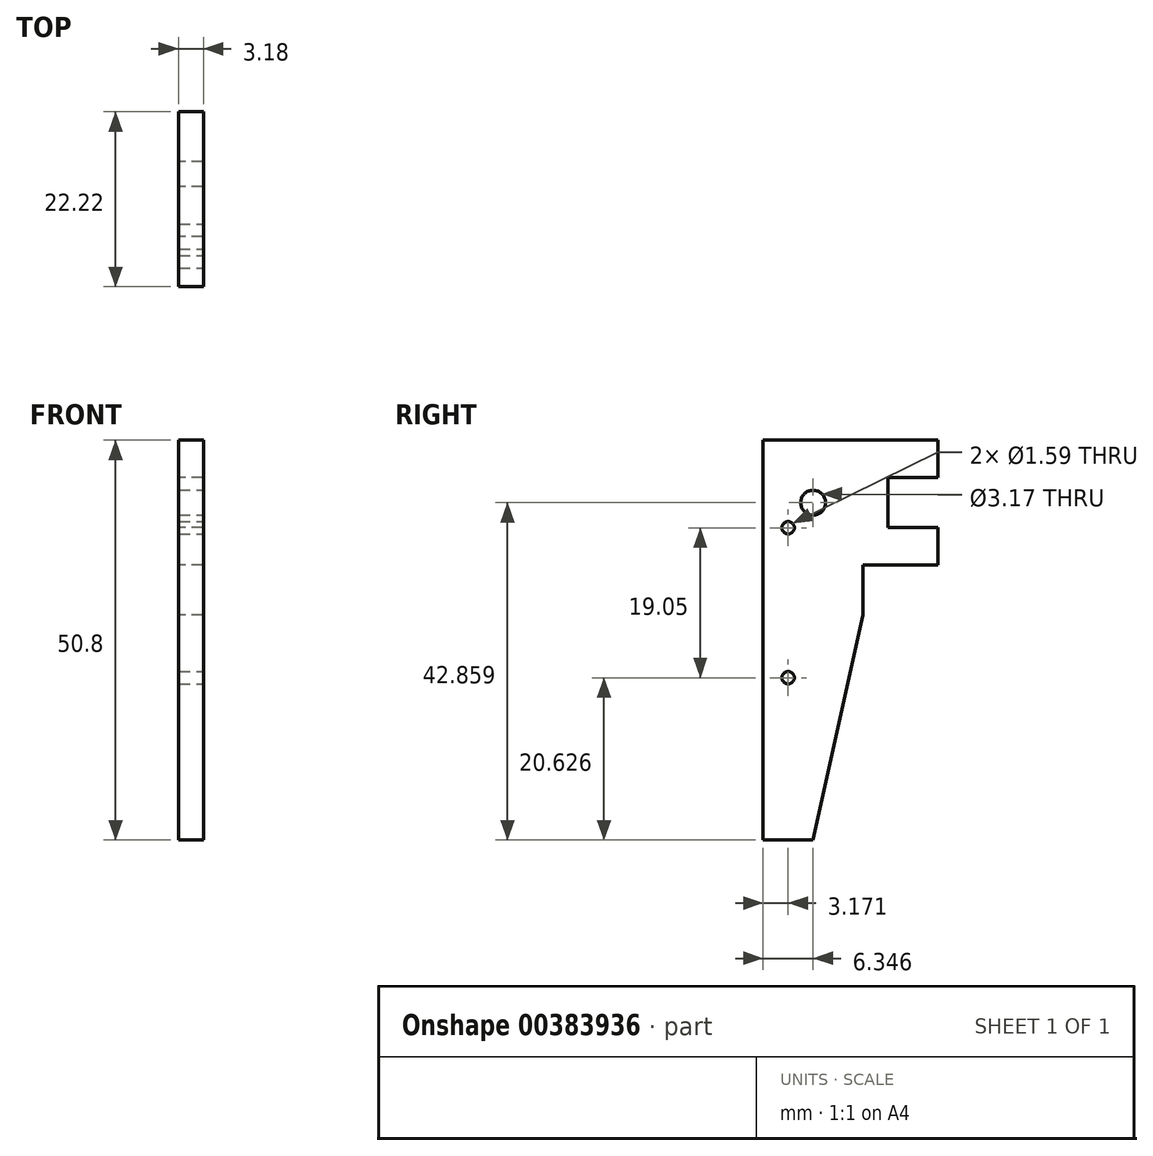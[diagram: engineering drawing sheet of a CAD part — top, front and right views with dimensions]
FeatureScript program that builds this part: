
annotation { "Feature Type Name" : "Feature", "Feature Type Description" : "" }
export const myFeature = defineFeature(function(context is Context, id is Id, definition is map)
    precondition{}
    {
        {
            var Q0;
            Q0=qCreatedBy(makeId("Right.planeOp"),FACE);
            var sketch = newSketch(context, id + "F0", { "sketchPlane" : qUnion([Q0])});
            skPoint(sketch, "E0.middle", {"position": v(-29.23, 59.86) * mm});
            skLineSegment(sketch, "E1", {"start": v(-22.88, 64.62) * mm, "end": v(-13.36, 64.62) * mm});
            skLineSegment(sketch, "E2", {"start": v(-13.36, 80.5) * mm, "end": v(-13.36, 75.73) * mm});
            skLineSegment(sketch, "E3", {"start": v(-13.36, 64.62) * mm, "end": v(-13.36, 69.38) * mm});
            skLineSegment(sketch, "E4", {"start": v(-13.36, 75.73) * mm, "end": v(-19.7, 75.73) * mm});
            skLineSegment(sketch, "E5", {"start": v(-13.36, 69.38) * mm, "end": v(-19.7, 69.38) * mm});
            skLineSegment(sketch, "E6", {"start": v(-19.7, 69.38) * mm, "end": v(-19.7, 75.73) * mm});
            skLineSegment(sketch, "E7", {"start": v(-22.88, 64.62) * mm, "end": v(-22.88, 58.27) * mm});
            skLineSegment(sketch, "E8", {"start": v(-22.88, 58.27) * mm, "end": v(-29.23, 29.7) * mm});
            skLineSegment(sketch, "E9", {"start": v(-35.58, 29.7) * mm, "end": v(-29.23, 29.7) * mm});
            skLineSegment(sketch, "E10", {"start": v(-35.58, 80.5) * mm, "end": v(-35.58, 29.7) * mm});
            skLineSegment(sketch, "E11", {"start": v(-35.58, 80.5) * mm, "end": v(-13.36, 80.5) * mm});
            skSolve(sketch);
        }
        {
            var Q0;
            Q0=qCreatedBy(makeId("Right.planeOp"),FACE);
            var sketch = newSketch(context, id + "F1", { "sketchPlane" : qUnion([Q0])});
            skCircle(sketch, "E12", {"center": v(-29.23, 72.56) * mm, "radius": 1.59 * mm});
            skCircle(sketch, "E13", {"center": v(-32.4, 50.33) * mm, "radius": 0.8 * mm});
            skCircle(sketch, "E14", {"center": v(-32.4, 69.38) * mm, "radius": 0.8 * mm});
            skSolve(sketch);
        }
        {
            var Q0;
            Q0 = qSketchRegion(id + "F0", true);
            extrude(context, id + "F2", {"entities" : qUnion([Q0]), "endBound" : BoundingType.SYMMETRIC, "depth" : 3.17 * mm});
        }
        {
            var Q0;
            Q0 = qSketchRegion(id + "F1", true);
            extrude(context, id + "F3", {"entities" : qUnion([Q0]), "operationType" : NewBodyOperationType.REMOVE, "endBound" : BoundingType.SYMMETRIC, "oppositeDirection" : true, "depth" : 25.4 * mm});
        }
    });
